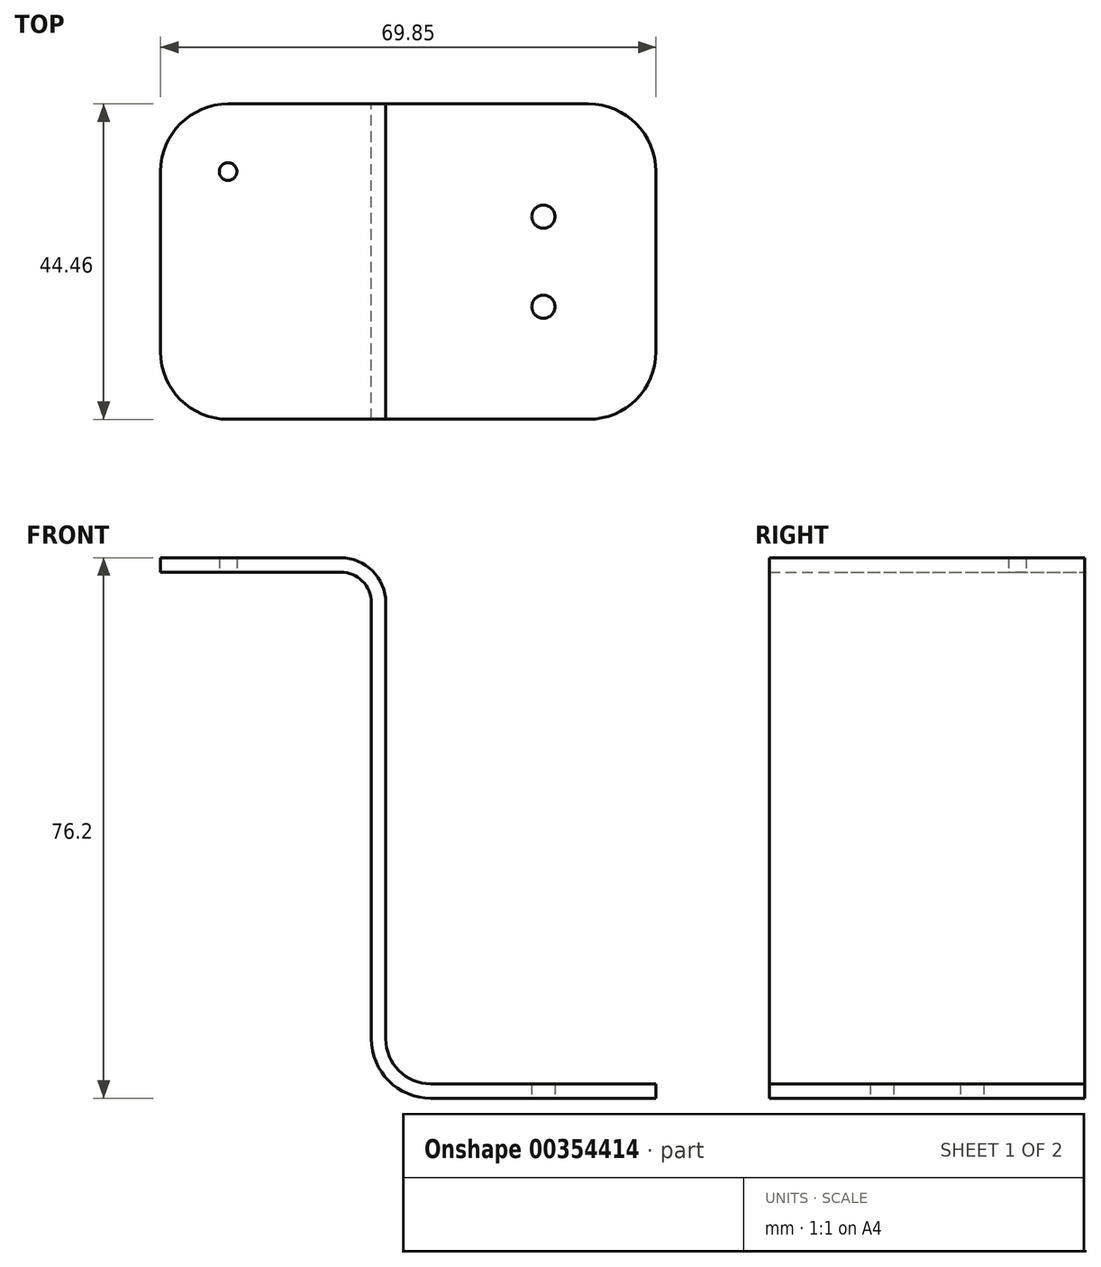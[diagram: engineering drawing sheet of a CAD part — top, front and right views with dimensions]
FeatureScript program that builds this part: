
annotation { "Feature Type Name" : "Feature", "Feature Type Description" : "" }
export const myFeature = defineFeature(function(context is Context, id is Id, definition is map)
    precondition{}
    {
        {
            var Q0;
            Q0=qCreatedBy(makeId("Front.planeOp"),FACE);
            var sketch = newSketch(context, id + "F0", { "sketchPlane" : qUnion([Q0])});
            skLineSegment(sketch, "E0", {"start": v(0, 29.72) * mm, "end": v(0, -31.75) * mm});
            skLineSegment(sketch, "E1", {"start": v(6.35, -38.1) * mm, "end": v(38.1, -38.1) * mm});
            skLineSegment(sketch, "E2", {"start": v(-6.35, 36.07) * mm, "end": v(-31.75, 36.07) * mm});
            skPoint(sketch, "E3.visualSharp", {"position": v(0, 36.07) * mm});
            skArc(sketch, "E3.filletArc", {"start": v(0, 29.72) * mm, "mid": v(-1.86, 34.2) * mm, "end": v(-6.35, 36.07) * mm});
            skPoint(sketch, "E4.visualSharp", {"position": v(0, -38.1) * mm});
            skArc(sketch, "E4.filletArc", {"start": v(0, -31.75) * mm, "mid": v(1.86, -36.24) * mm, "end": v(6.35, -38.1) * mm});
            skLineSegment(sketch, "E5.0", {"start": v(-6.35, 34.03) * mm, "end": v(-31.75, 34.03) * mm});
            skLineSegment(sketch, "E6.0", {"start": v(-2.03, 29.72) * mm, "end": v(-2.03, -31.75) * mm});
            skLineSegment(sketch, "E7.0", {"start": v(6.35, -40.13) * mm, "end": v(38.1, -40.13) * mm});
            skArc(sketch, "E8", {"start": v(-2.03, -31.75) * mm, "mid": v(0.42, -37.68) * mm, "end": v(6.35, -40.13) * mm});
            skArc(sketch, "E9", {"start": v(-6.35, 34.03) * mm, "mid": v(-3.3, 32.77) * mm, "end": v(-2.03, 29.72) * mm});
            skLineSegment(sketch, "E10", {"start": v(-31.75, 36.07) * mm, "end": v(-31.75, 34.03) * mm});
            skLineSegment(sketch, "E11", {"start": v(38.1, -38.1) * mm, "end": v(38.1, -40.13) * mm});
            skSolve(sketch);
        }
        {
            var Q0;
            Q0 = qSketchRegion(id + "F0", true);
            extrude(context, id + "F1", {"entities" : qUnion([Q0]), "depth" : 22.22 * mm, "hasSecondDirection" : true, "secondDirectionOppositeDirection" : true, "secondDirectionDepth" : 22.22 * mm});
        }
        {
            var Q0;
            Q0=makeQuery(id+"F1.opExtrude","CAP_EDGE",EDGE,{"disambiguationData":[OSD([sQuery(id+"F0.wireOp",EDGE,"E10")])],"isStart":false});
            var Q1;
            Q1=makeQuery(id+"F1.opExtrude","CAP_EDGE",EDGE,{"disambiguationData":[OSD([sQuery(id+"F0.wireOp",EDGE,"E10")])],"isStart":true});
            var Q2;
            Q2=makeQuery(id+"F1.opExtrude","CAP_EDGE",EDGE,{"disambiguationData":[OSD([sQuery(id+"F0.wireOp",EDGE,"E11")])],"isStart":false});
            var Q3;
            Q3=makeQuery(id+"F1.opExtrude","CAP_EDGE",EDGE,{"disambiguationData":[OSD([sQuery(id+"F0.wireOp",EDGE,"E11")])],"isStart":true});
            fillet(context, id + "F2", {"entities" : qUnion([Q0, Q1, Q2, Q3]), "radius" : 9.52 * mm, "tangentPropagation" : true, "allowEdgeOverflow" : false});
        }
        {
            var Q0;
            Q0=makeQuery(id+"F1.opExtrude","SWEPT_FACE",FACE,{"disambiguationData":[OSD([sQuery(id+"F0.wireOp",EDGE,"E5.0")])]});
            var sketch = newSketch(context, id + "F3", { "sketchPlane" : qUnion([Q0])});
            skCircle(sketch, "E12", {"center": v(-22.22, -12.7) * mm, "radius": 0.77 * mm});
            skSolve(sketch);
        }
        {
            var Q0;
            Q0=sQuery(id+"F3.wireOp",VERTEX,"E12.center");
            var Q1;
            Q1=makeQuery(id+"F1.opExtrude","SWEPT_BODY",BODY,{"disambiguationData":[OSD([sQuery(id+"F0.wireOp",EDGE,"E0"),sQuery(id+"F0.wireOp",EDGE,"E1"),sQuery(id+"F0.wireOp",EDGE,"E2"),sQuery(id+"F0.wireOp",EDGE,"E3.filletArc"),sQuery(id+"F0.wireOp",EDGE,"E4.filletArc"),sQuery(id+"F0.wireOp",EDGE,"E5.0"),sQuery(id+"F0.wireOp",EDGE,"E6.0"),sQuery(id+"F0.wireOp",EDGE,"E7.0"),sQuery(id+"F0.wireOp",EDGE,"E8"),sQuery(id+"F0.wireOp",EDGE,"E9"),sQuery(id+"F0.wireOp",EDGE,"E10"),sQuery(id+"F0.wireOp",EDGE,"E11")])]});
            hole(context, id + "F4", {"style" : HoleStyle.SIMPLE, "endStyle" : HoleEndStyle.THROUGH, "holeDiameter" : 2.5 * mm, "isTappedThrough" : true, "tappedDepth" : 12.7 * mm, "tapClearance" : 3, "startFromSketch" : true, "locations" : qUnion([Q0]), "scope" : qUnion([Q1])});
        }
        {
            var Q0;
            Q0=makeQuery(id+"F1.opExtrude","SWEPT_FACE",FACE,{"disambiguationData":[OSD([sQuery(id+"F0.wireOp",EDGE,"E7.0")])]});
            var sketch = newSketch(context, id + "F5", { "sketchPlane" : qUnion([Q0])});
            skCircle(sketch, "E13", {"center": v(22.22, -6.35) * mm, "radius": 1.63 * mm});
            skCircle(sketch, "E14.MirrorC", {"center": v(22.22, 6.35) * mm, "radius": 1.63 * mm});
            skSolve(sketch);
        }
        {
            var Q0;
            Q0=sQuery(id+"F5.wireOp",VERTEX,"E14.MirrorC.center");
            var Q1;
            Q1=sQuery(id+"F5.wireOp",VERTEX,"E13.center");
            var Q2;
            Q2=makeQuery(id+"F1.opExtrude","SWEPT_BODY",BODY,{"disambiguationData":[OSD([sQuery(id+"F0.wireOp",EDGE,"E0"),sQuery(id+"F0.wireOp",EDGE,"E1"),sQuery(id+"F0.wireOp",EDGE,"E2"),sQuery(id+"F0.wireOp",EDGE,"E3.filletArc"),sQuery(id+"F0.wireOp",EDGE,"E4.filletArc"),sQuery(id+"F0.wireOp",EDGE,"E5.0"),sQuery(id+"F0.wireOp",EDGE,"E6.0"),sQuery(id+"F0.wireOp",EDGE,"E7.0"),sQuery(id+"F0.wireOp",EDGE,"E8"),sQuery(id+"F0.wireOp",EDGE,"E9"),sQuery(id+"F0.wireOp",EDGE,"E10"),sQuery(id+"F0.wireOp",EDGE,"E11")])]});
            hole(context, id + "F6", {"style" : HoleStyle.SIMPLE, "endStyle" : HoleEndStyle.THROUGH, "holeDiameter" : 3.26 * mm, "isTappedThrough" : true, "tappedDepth" : 12.7 * mm, "tapClearance" : 3, "startFromSketch" : true, "locations" : qUnion([Q0, Q1]), "scope" : qUnion([Q2])});
        }
    });
